# Revit family: 609551001_Asiento Sanitario Forte AroAlongado
name_source: partatom
category: Plumbing Fixtures
units: mm (PartAtom-declared; Revit-internal decimal feet)

## family parameters
Always vertical = Yes
Cut with Voids When Loaded = No
OmniClass Number = 23.31.19.19.17
Part Type = Normal
Room Calculation Point = No
Round Connector Dimension = Use Diameter
Shared = No
Work Plane-Based = No

## types (1)
- 609551001_Asiento Sanitario Forte AroAlongado
    Alto = 58 mm  [stored 0.190289 ft]
    Ancho = 366 mm
    Angulos de detencion = Entre 79° - 101°
    Creado por = BIMBAU
    Default Elevation = 0 mm  [stored 0 ft]
    Description = Asiento Standard
    Fecha de creación = 11/03/2021
    Garantía = 5 años
    Manufacturer = Corona
    Material = Corona_Polipropileno
    Material 2 = Corona_Acero inoxidable
    Model = Asiento Sanitario Forte Aro Alongado
    Peso  Bruto = 1,60 grs.
    Peso neto = 1,25 grs.
    Profundidad = 468 mm  [stored 1.53543 ft]
    Referencia = 609551001
    Resistencia de flexion = 1335 ± 22 N - 300 ± 5 lbs.
    SKU = 609551001
    URL = https://bimbau.s3.amazonaws.com

note: [stored X ft] marks values corroborated as IEEE doubles in the binary element streams (Revit-internal decimal feet)

## geometry (parser evidence)
native form markers: Sweep x3
no freeform markers — native parametric forms only
